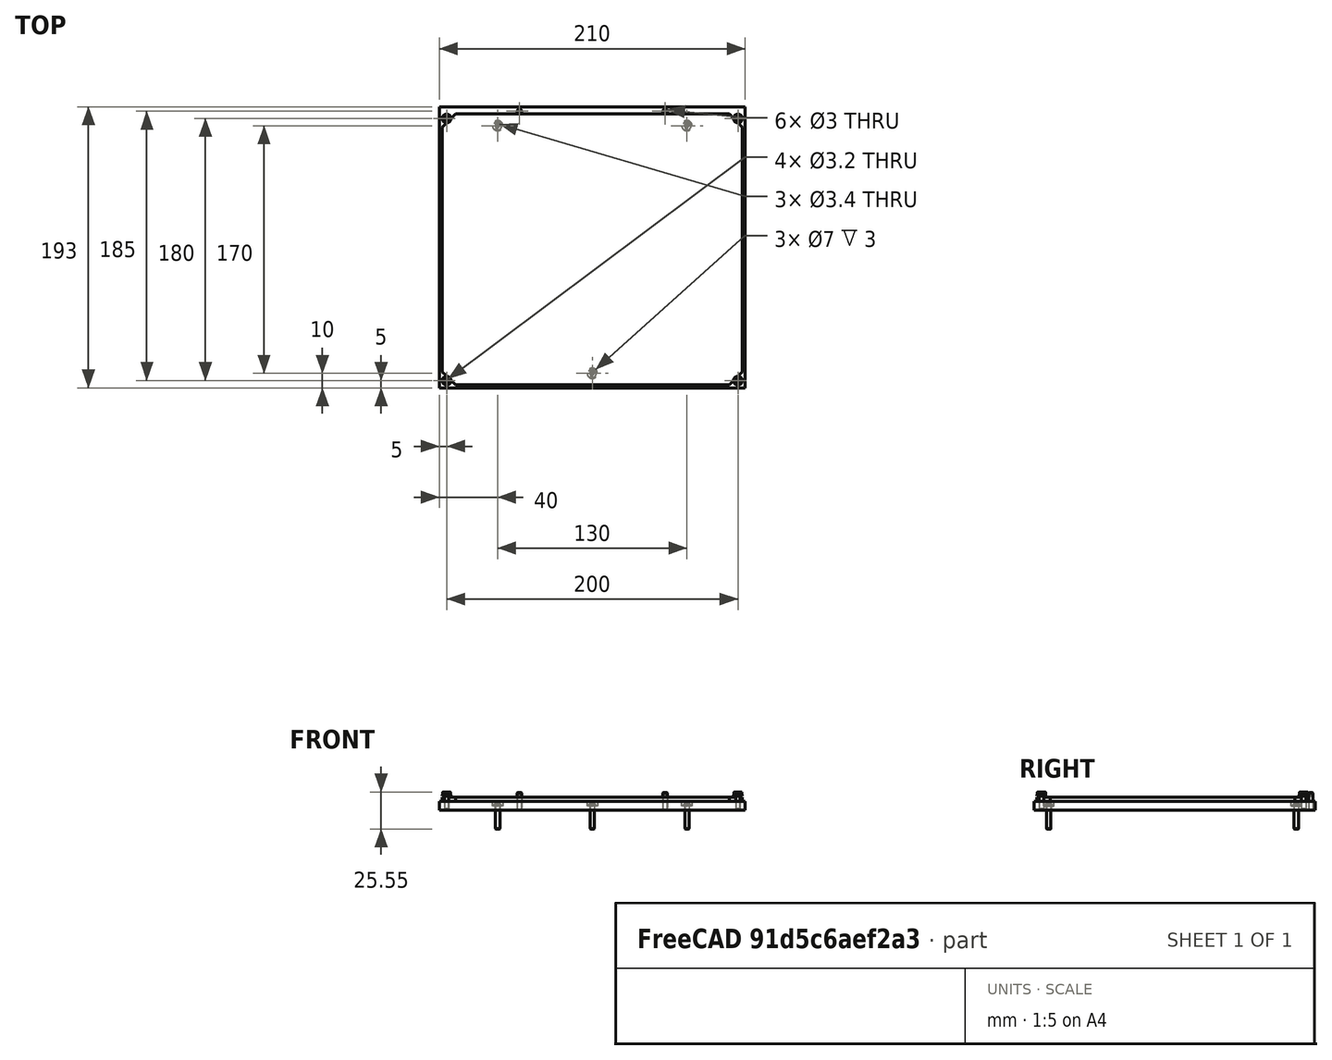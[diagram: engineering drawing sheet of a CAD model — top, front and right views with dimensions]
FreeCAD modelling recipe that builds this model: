
FCSTD DOCUMENT  (FreeCAD 0.19R24291 (Git))
Label: 180-glass-bed-assembly
License: Other
LicenseURL: GPL3
objects: Part::FeaturePython×13, Part::Feature×2, App::Part×1
note: 15 computed .brp shape members not serialized (recipe doc carries the construction recipe); baked Part::Feature solids carry a one-line shape summary decoded from their .brp

FEATURE [Part::Feature] Pocket002  label="180-aluminum-plate"
  shape: bbox 210 x 193 x 6 mm, 21 faces (baked)
FEATURE [Part::Feature] Chamfer002  label="180-glass-plate"
  Placement = pos=(0,0,6) rot=(0,0,1;0rad)
  shape: bbox 206 x 186 x 3 mm, 10 faces (baked)
FEATURE [Part::FeaturePython] Screw  label="M3x16-Screw"  # Fasteners workbench fastener (typed FeaturePython)
  Placement = pos=(0,-85,3) rot=(0,0,1;0rad)
  baseObject = -> Pocket002 [Edge36]
  diameter = 1
  invert = true
  length = 5
  lengthCustom = 16
  matchOuter = true
  offset = 0
  thread = false
  type = 40
FEATURE [Part::FeaturePython] Screw001  label="M3x16-Screw001"  # Fasteners workbench fastener (typed FeaturePython)
  Placement = pos=(-65,85,3) rot=(0,0,1;0rad)
  baseObject = -> Pocket002 [Edge34]
  diameter = 1
  invert = true
  length = 5
  lengthCustom = 16
  matchOuter = true
  offset = 0
  thread = false
  type = 40
FEATURE [Part::FeaturePython] Screw002  label="M3x16-Screw002"  # Fasteners workbench fastener (typed FeaturePython)
  Placement = pos=(65,85,3) rot=(0,0,1;0rad)
  baseObject = -> Pocket002 [Edge32]
  diameter = 1
  invert = true
  length = 5
  lengthCustom = 16
  matchOuter = true
  offset = 0
  thread = false
  type = 40
FEATURE [Part::FeaturePython] Screw003  label="M3x12-Screw"  # Fasteners workbench fastener (typed FeaturePython)
  Placement = pos=(-50,95,12) rot=(0,0,1;0rad)
  baseObject = -> Pocket002 [Edge28]
  diameter = 6
  invert = false
  length = 7
  lengthCustom = 12
  matchOuter = true
  offset = 6
  thread = false
  type = 30
FEATURE [Part::FeaturePython] Screw004  label="M3x12-Screw001"  # Fasteners workbench fastener (typed FeaturePython)
  Placement = pos=(50,95,12) rot=(0,0,1;0rad)
  baseObject = -> Pocket002 [Edge27]
  diameter = 6
  invert = false
  length = 7
  lengthCustom = 12
  matchOuter = true
  offset = 6
  thread = false
  type = 30
FEATURE [Part::FeaturePython] Washer  label="M3-Silicon-Washer"  # Fasteners workbench fastener (typed FeaturePython)
  Placement = pos=(-100,90,10) rot=(0,0,1;0rad)
  baseObject = -> Pocket002 [Edge30]
  diameter = 4
  invert = false
  matchOuter = true
  offset = 4
  type = 5
FEATURE [Part::FeaturePython] Washer001  label="M3-Silicon-Washer001"  # Fasteners workbench fastener (typed FeaturePython)
  Placement = pos=(100,90,10) rot=(0,0,1;0rad)
  baseObject = -> Pocket002 [Edge25]
  diameter = 4
  invert = false
  matchOuter = true
  offset = 4
  type = 5
FEATURE [Part::FeaturePython] Washer002  label="M3-Silicon-Washer002"  # Fasteners workbench fastener (typed FeaturePython)
  Placement = pos=(100,-90,10) rot=(0,0,1;0rad)
  baseObject = -> Pocket002 [Edge22]
  diameter = 4
  invert = false
  matchOuter = true
  offset = 4
  type = 5
FEATURE [Part::FeaturePython] Washer003  label="M3-Silicon-Washer003"  # Fasteners workbench fastener (typed FeaturePython)
  Placement = pos=(-100,-90,10) rot=(0,0,1;0rad)
  baseObject = -> Pocket002 [Edge24]
  diameter = 4
  invert = false
  matchOuter = true
  offset = 4
  type = 5
FEATURE [Part::FeaturePython] Screw005  label="M3x10-low-head Screw"  # Fasteners workbench fastener (typed FeaturePython)
  Placement = pos=(-100,-90,10.55) rot=(0,0,1;0rad)
  baseObject = -> Washer003 [Edge1]
  diameter = 1
  invert = false
  length = 3
  lengthCustom = 10
  matchOuter = true
  offset = 0
  thread = false
  type = 14
FEATURE [Part::FeaturePython] Screw006  label="M3x10-low-head Screw001"  # Fasteners workbench fastener (typed FeaturePython)
  Placement = pos=(100,-90,10.55) rot=(0,0,1;0rad)
  baseObject = -> Washer002 [Edge1]
  diameter = 1
  invert = false
  length = 3
  lengthCustom = 10
  matchOuter = true
  offset = 0
  thread = false
  type = 14
FEATURE [Part::FeaturePython] Screw007  label="M3x10-low-head Screw002"  # Fasteners workbench fastener (typed FeaturePython)
  Placement = pos=(100,90,10.55) rot=(0,0,1;0rad)
  baseObject = -> Washer001 [Edge1]
  diameter = 1
  invert = false
  length = 3
  lengthCustom = 10
  matchOuter = true
  offset = 0
  thread = false
  type = 14
FEATURE [Part::FeaturePython] Screw008  label="M3x10-low-head Screw003"  # Fasteners workbench fastener (typed FeaturePython)
  Placement = pos=(-100,90,10.55) rot=(0,0,1;0rad)
  baseObject = -> Washer [Edge1]
  diameter = 1
  invert = false
  length = 3
  lengthCustom = 10
  matchOuter = true
  offset = 0
  thread = false
  type = 14
FEATURE [App::Part] Part  label="180-glass-bed"
  Group = -> [Chamfer002,Pocket002,Screw,Screw001,Screw002,Screw003,Screw004,Washer,Washer001,Washer002,Washer003,Screw005,Screw006,Screw007,Screw008]
  Origin = -> Origin
